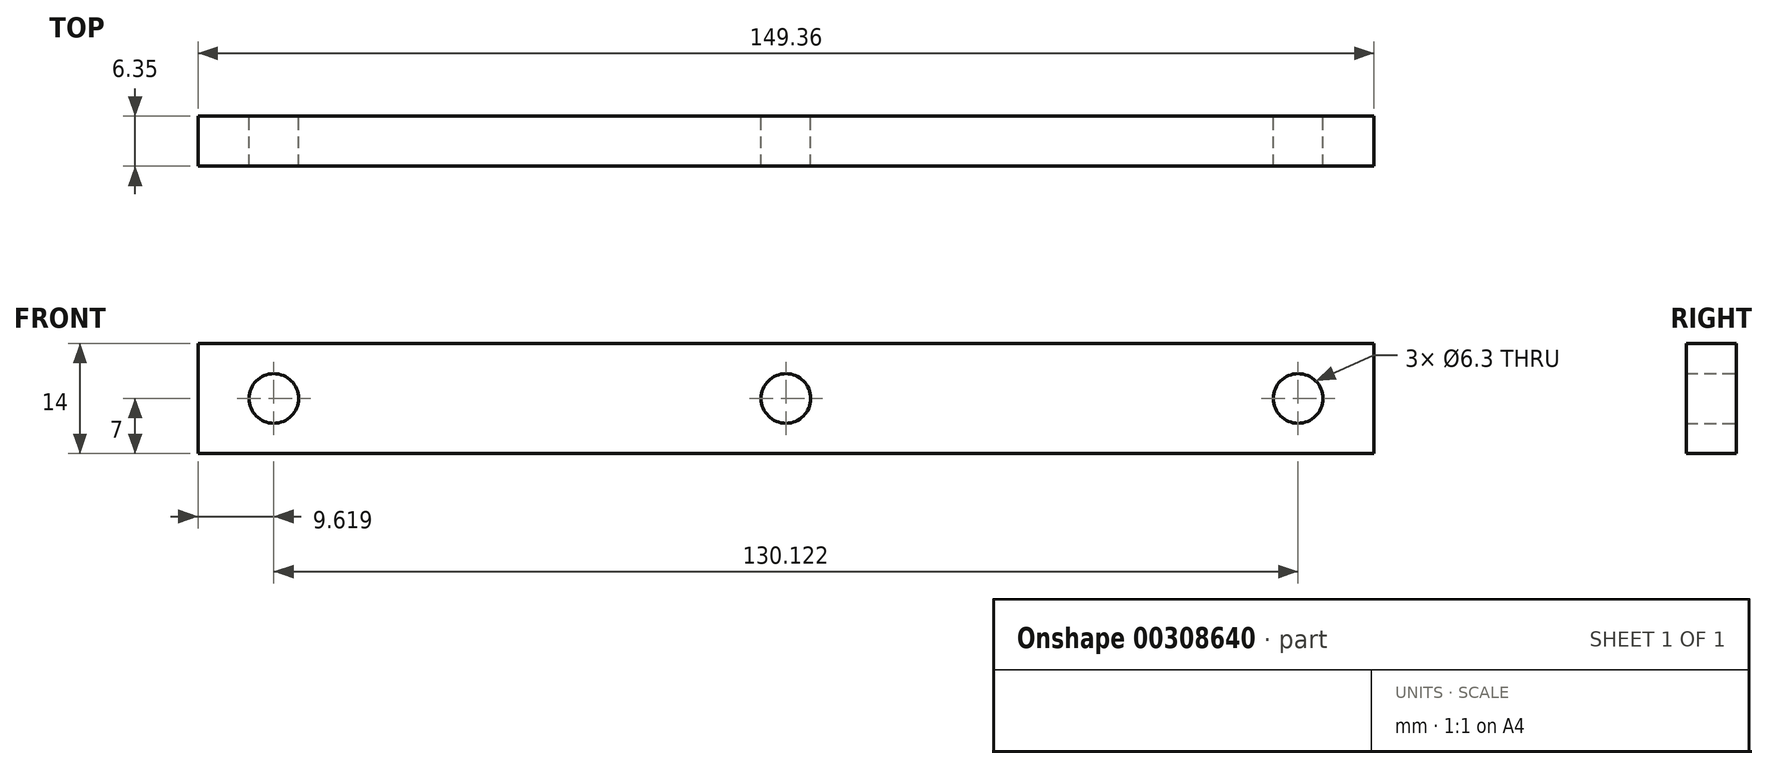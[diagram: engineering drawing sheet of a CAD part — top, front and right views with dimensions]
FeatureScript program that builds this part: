
annotation { "Feature Type Name" : "Feature", "Feature Type Description" : "" }
export const myFeature = defineFeature(function(context is Context, id is Id, definition is map)
    precondition{}
    {
        {
            var Q0;
            Q0=qCreatedBy(makeId("Front.planeOp"),FACE);
            var sketch = newSketch(context, id + "F0", { "sketchPlane" : qUnion([Q0])});
            skLineSegment(sketch, "E0.0", {"start": v(0, 7) * mm, "end": v(-74.68, 7) * mm});
            skLineSegment(sketch, "E1.0", {"start": v(0, -7) * mm, "end": v(-74.68, -7) * mm});
            skLineSegment(sketch, "E2", {"start": v(-74.68, 0) * mm, "end": v(-74.68, 7) * mm});
            skLineSegment(sketch, "E3", {"start": v(-74.68, -7) * mm, "end": v(-74.68, 0) * mm});
            skCircle(sketch, "E4", {"center": v(-65.06, 0) * mm, "radius": 3.15 * mm});
            skLineSegment(sketch, "E5.MirrorCS", {"start": v(74.68, 0) * mm, "end": v(74.68, 7) * mm});
            skLineSegment(sketch, "E6.MirrorCS", {"start": v(74.68, -7) * mm, "end": v(74.68, 0) * mm});
            skCircle(sketch, "E7.MirrorC", {"center": v(65.06, 0) * mm, "radius": 3.15 * mm});
            skLineSegment(sketch, "E8.MirrorCS", {"start": v(0, 7) * mm, "end": v(74.68, 7) * mm});
            skLineSegment(sketch, "E9.MirrorCS", {"start": v(0, -7) * mm, "end": v(74.68, -7) * mm});
            skCircle(sketch, "E10", {"center": v(0, 0) * mm, "radius": 3.15 * mm});
            skSolve(sketch);
        }
        {
            var Q0;
            Q0=makeQuery(id+"F0.imprint","IMPRINT",FACE,{"disambiguationData":[TD([[makeQuery(id+"F0.imprint","IMPRINT",EDGE,{"derivedFrom":sQuery(id+"F0.wireOp",EDGE,"E0.0")}),1.0]])]});
            extrude(context, id + "F1", {"entities" : qUnion([Q0]), "depth" : 6.35 * mm});
        }
    });
